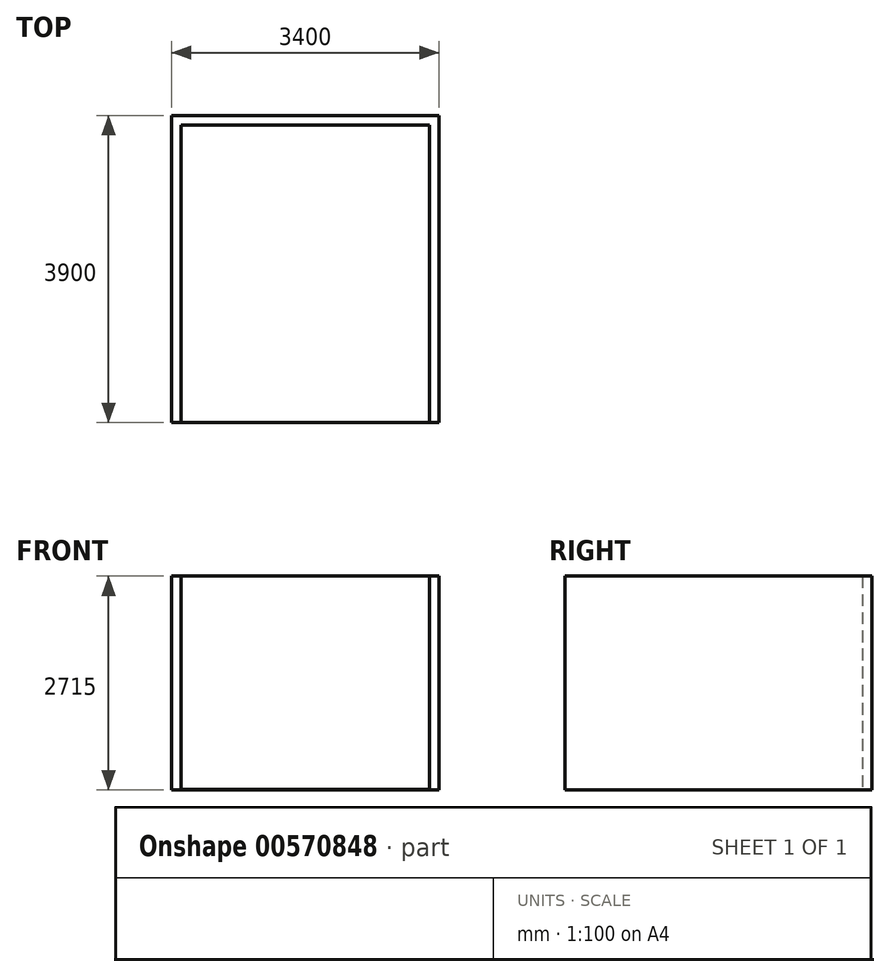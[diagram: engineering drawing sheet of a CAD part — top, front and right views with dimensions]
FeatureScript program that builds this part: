
annotation { "Feature Type Name" : "Feature", "Feature Type Description" : "" }
export const myFeature = defineFeature(function(context is Context, id is Id, definition is map)
    precondition{}
    {
        {
            var Q0;
            Q0=qCreatedBy(makeId("Top.planeOp"),FACE);
            var sketch = newSketch(context, id + "F0", { "sketchPlane" : qUnion([Q0])});
            skLineSegment(sketch, "E0.bottom", {"start": v(0, 0) * mm, "end": v(-3400, 0) * mm});
            skLineSegment(sketch, "E0.top", {"start": v(0, 3900) * mm, "end": v(-3400, 3900) * mm});
            skLineSegment(sketch, "E0.left", {"start": v(0, 0) * mm, "end": v(0, 3900) * mm});
            skLineSegment(sketch, "E0.right", {"start": v(-3400, 0) * mm, "end": v(-3400, 3900) * mm});
            skSolve(sketch);
        }
        {
            var Q0;
            Q0 = qSketchRegion(id + "F0", true);
            extrude(context, id + "F1", {"entities" : qUnion([Q0]), "depth" : 5 * mm, "offsetDistance" : 25 * mm});
        }
        {
            var Q0;
            Q0=makeQuery(id+"F1.opExtrude","CAP_FACE",FACE,{"disambiguationData":[OSD([sQuery(id+"F0.wireOp",EDGE,"E0.bottom"),sQuery(id+"F0.wireOp",EDGE,"E0.top"),sQuery(id+"F0.wireOp",EDGE,"E0.left"),sQuery(id+"F0.wireOp",EDGE,"E0.right")])],"isStart":false});
            var sketch = newSketch(context, id + "F2", { "sketchPlane" : qUnion([Q0])});
            skLineSegment(sketch, "E1.bottom", {"start": v(0, 3900) * mm, "end": v(-3400, 3900) * mm});
            skLineSegment(sketch, "E1.top", {"start": v(-120, 3780) * mm, "end": v(-3280, 3780) * mm});
            skLineSegment(sketch, "E1.left", {"start": v(0, 3900) * mm, "end": v(0, 3780) * mm});
            skLineSegment(sketch, "E1.right", {"start": v(-3400, 3900) * mm, "end": v(-3400, 3780) * mm});
            skLineSegment(sketch, "E2.top", {"start": v(-3400, 0) * mm, "end": v(-3280, 0) * mm});
            skLineSegment(sketch, "E2.left", {"start": v(-3400, 3780) * mm, "end": v(-3400, 0) * mm});
            skLineSegment(sketch, "E2.right", {"start": v(-3280, 3780) * mm, "end": v(-3280, 0) * mm});
            skLineSegment(sketch, "E3.top", {"start": v(0, 0) * mm, "end": v(-120, 0) * mm});
            skLineSegment(sketch, "E3.left", {"start": v(0, 3780) * mm, "end": v(0, 0) * mm});
            skLineSegment(sketch, "E3.right", {"start": v(-120, 3780) * mm, "end": v(-120, 0) * mm});
            skSolve(sketch);
        }
        {
            var Q0;
            Q0 = qSketchRegion(id + "F2", true);
            extrude(context, id + "F3", {"entities" : qUnion([Q0]), "operationType" : NewBodyOperationType.ADD, "depth" : 2710 * mm, "offsetDistance" : 25 * mm});
        }
    });
